# Revit family: NBS_BetafenceLimited_MtlMeshPnlFncngSym_Securifor2D-BekafixSuper
name_source: partatom
category: Site
revit_build: Autodesk Revit 2017 (Build: 20171027_0315(x64)
units: mm (PartAtom-declared; Revit-internal decimal feet)

## family parameters
Cut with Voids When Loaded = No
Part Type = Normal
Round Connector Dimension = Use Diameter
Shared = No

## types (1)
- Securifor 2D + Bekafix Super
    Applications = Energy and resources, high security,  infra-structure and transport, public spaces and buildings
    AssetType = Fixed
    BIMObjectName = NBS_BetafenceLimited_MetalMeshPanelFencingSystem_Securifor2D-BekafixSuper
    Category = Ss_25_14_67_51: Metal mesh panel fencing systems
    Color = Green (RAL 6005)
    Description = Perimeter security
    Diameter = 0 mm  [stored 0 ft]
    DurationUnit = year
    FoundationMaterial = NBS_Concept
    Functionalities = Dissuasion, delay
    Gradient01Maximum = 3.98%
    Gradient01PostAxisDistance = 2515 mm  [stored 8.25131 ft]
    Gradient02Maximum = 5.97%
    Gradient02PostAxisDistance = 1676 mm
    Gradient03Maximum = 8.20%
    Gradient03PostAxisDistance = 1219 mm
    Gradient04Maximum = 12.00%
    Gradient04PostAxisDistance = 838 mm
    GradientMaximumPostAxisDistance = 838 mm
    Height = 3048 mm  [stored 10 ft]
    IfcExportAs = IfcWallType
    IfcExportType = NOTDEFINED
    IsExternal = Yes
    ManufacturerName = Betafence Limited
    ManufacturerURL = www.betafence.co.uk
    MaximumIncline = 12.00%
    ModelReference = Securifor 2D Bekafix Super
    NBSCertification = www.nationalbimlibrary.com/cert/3ujsl30s
    NBSDescription = Metal mesh panel fencing system
    NBSReference = 25-20-30/145
    Name = MetalMeshPanelFencingSystem_Securifor2DBekafixSuper_BetafenceLimited
    NominalHeight = 3048 mm  [stored 10 ft]
    NominalLength = 0 mm  [stored 0 ft]
    NominalWidth = 2544 mm
    PanelElevationAboveFoundation = 30 mm  [stored 0.0984252 ft]
    PanelHeight = 3048 mm  [stored 10 ft]
    PanelMaterial = NBS_BetafenceLimited_MtlMeshPnlFncngSym_Securifor2D_Panel
    PanelOffsetFromPost = 12 mm  [stored 0.0393701 ft]
    PanelOffsetFromPostCL = 5 mm  [stored 0.0164042 ft]
    PanelSizeOptions = 2520.6 x 1985.2 mm, 2520.6 x 2442.4 mm, 2520.6 x 3052 mm
    PanelThickness = 10 mm  [stored 0.0328084 ft]
    PostFoundations = Installation guides available on request
    PostHeightAboveGround = 2878 mm  [stored 9.44226 ft]
    PostHeightBelowGround = 200 mm  [stored 0.656168 ft]
    PostMaterial = NBS_Concept
    PostThickness = 70 mm  [stored 0.229659 ft]
    PostWidth = 44 mm  [stored 0.144357 ft]
    Posts = Bekafix super
    ProductInformation = //www.betafence.co.uk/en/securifor-2d-0
    SecurityLevel = High security
    StandardPostAxisDistance = 2544 mm
    Uniclass2015Code = Ss_25_14_67_51
    Uniclass2015Title = Metal mesh panel fencing systems
    Uniclass2015Version = Systems v1.13
    Version = 2
    WarrantyDurationUnit = year

note: [stored X ft] marks values corroborated as IEEE doubles in the binary element streams (Revit-internal decimal feet)

## geometry (parser evidence)
native form markers: Sweep x7
no freeform markers — native parametric forms only
